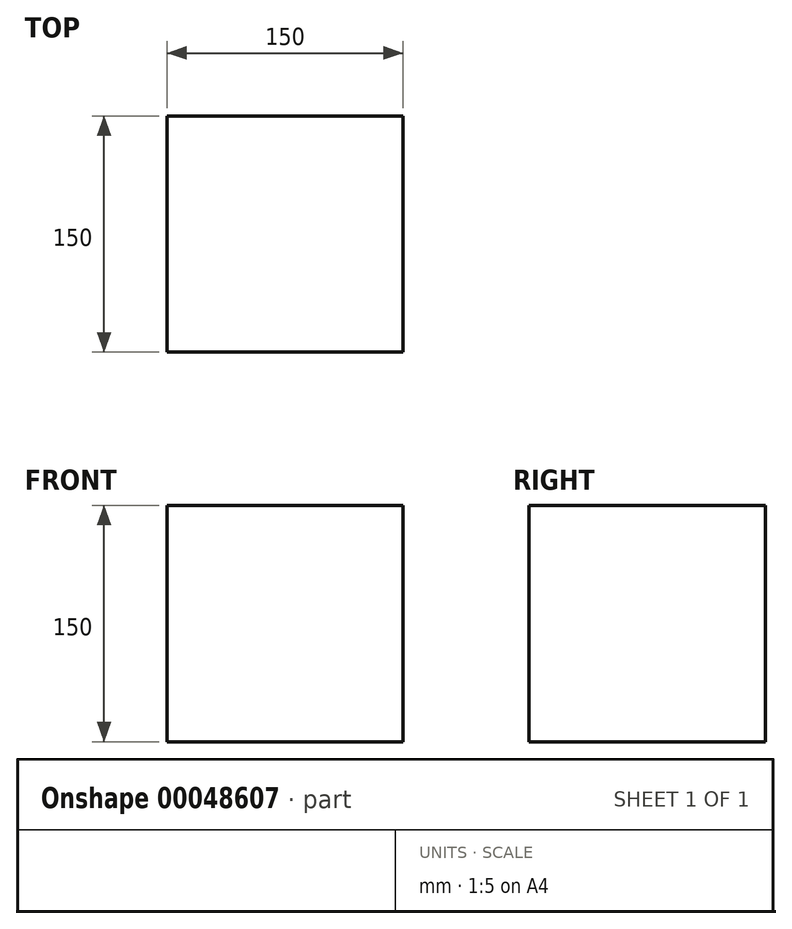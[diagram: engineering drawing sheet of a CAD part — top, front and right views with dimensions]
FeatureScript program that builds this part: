
annotation { "Feature Type Name" : "Feature", "Feature Type Description" : "" }
export const myFeature = defineFeature(function(context is Context, id is Id, definition is map)
    precondition{}
    {
        {
            var Q0;
            Q0=qCreatedBy(makeId("Top.planeOp"),FACE);
            var sketch = newSketch(context, id + "F0", { "sketchPlane" : qUnion([Q0])});
            skLineSegment(sketch, "E0.rect.bottom", {"start": v(-75, 75) * mm, "end": v(75, 75) * mm});
            skLineSegment(sketch, "E0.rect.top", {"start": v(-75, -75) * mm, "end": v(75, -75) * mm});
            skLineSegment(sketch, "E0.rect.left", {"start": v(-75, 75) * mm, "end": v(-75, -75) * mm});
            skLineSegment(sketch, "E0.rect.right", {"start": v(75, 75) * mm, "end": v(75, -75) * mm});
            skPoint(sketch, "E0.rect.middle", {"position": v(0, 0) * mm});
            skSolve(sketch);
        }
        {
            var Q0;
            Q0=makeQuery(id+"F0.imprint","IMPRINT",FACE,{"disambiguationData":[TD([[makeQuery(id+"F0.imprint","IMPRINT",EDGE,{"derivedFrom":sQuery(id+"F0.wireOp",EDGE,"E0.rect.bottom")}),-1.0]])]});
            extrude(context, id + "F1", {"entities" : qUnion([Q0]), "depth" : 150 * mm});
        }
    });
